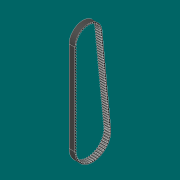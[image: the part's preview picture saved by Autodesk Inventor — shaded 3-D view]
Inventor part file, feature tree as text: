
AUTODESK INVENTOR PART (.ipt)
format: ipt  version: 2016 (Build 200138000, 138)  size: 1,610,752 bytes
history: native  units: mm
features: sketch x6, extrude x3, other x2, pattern_linear x1
ambient origin geometry x8: Origin, YZ Plane, XZ Plane, XY Plane, X Axis, Y Axis, Z Axis, Center Point
bodies: Solid1 (feature_tree)
feature tree (12):
  other  "<userpath>\oneDrive\projects\splitFlapDisplay\parameters.xlsx"
  extrude  "Extrusion1"  Depth=1.0mm
  pattern_linear  "Rectangular Pattern1"  Spacing1=5.0mm  [1 undecoded]
  sketch  "Sketch2"  dims[d11=0.555mm]
  other  "Bend Part1"
  extrude  "Extrusion2"  Depth=1200.0mm
  extrude  "Extrusion4"  Depth=15.402264mm
  sketch  "Sketch1"  dims[d9=1.0mm d10=1.0mm]
  sketch  "Sketch3"  dims[d13=0.8mm]
  sketch  "Sketch4"  dims[d14=0.15mm]
  sketch  "Sketch14"  dims[d15=0.15mm]
  sketch  "Sketch16"  dims[d16=0.75mm d20=5.0mm d21=0.0mm d22=1200.0mm d24=2.0mm d28=15.402264mm d29=32.389455mm d41=0.254mm d42=0.75mm d43=1.38mm d44=1.0mm d45=2.0mm d46=5.0mm d63=84.943068mm d67=11.63428mm d68=30.442398mm d69=16.274214mm d73=17.1327mm d74=32.698074mm d76=70.359822mm d77=80.84mm d85=77.347685mm d90=10.0mm d91=0.0mm d95=0.01mm d96=10.0mm d97=0.0mm]
note: 1 required parameter value undecoded (feature->parameter linkage not recoverable at this tier; creation-order binding heuristic only, values carry confidence <= 0.55)
